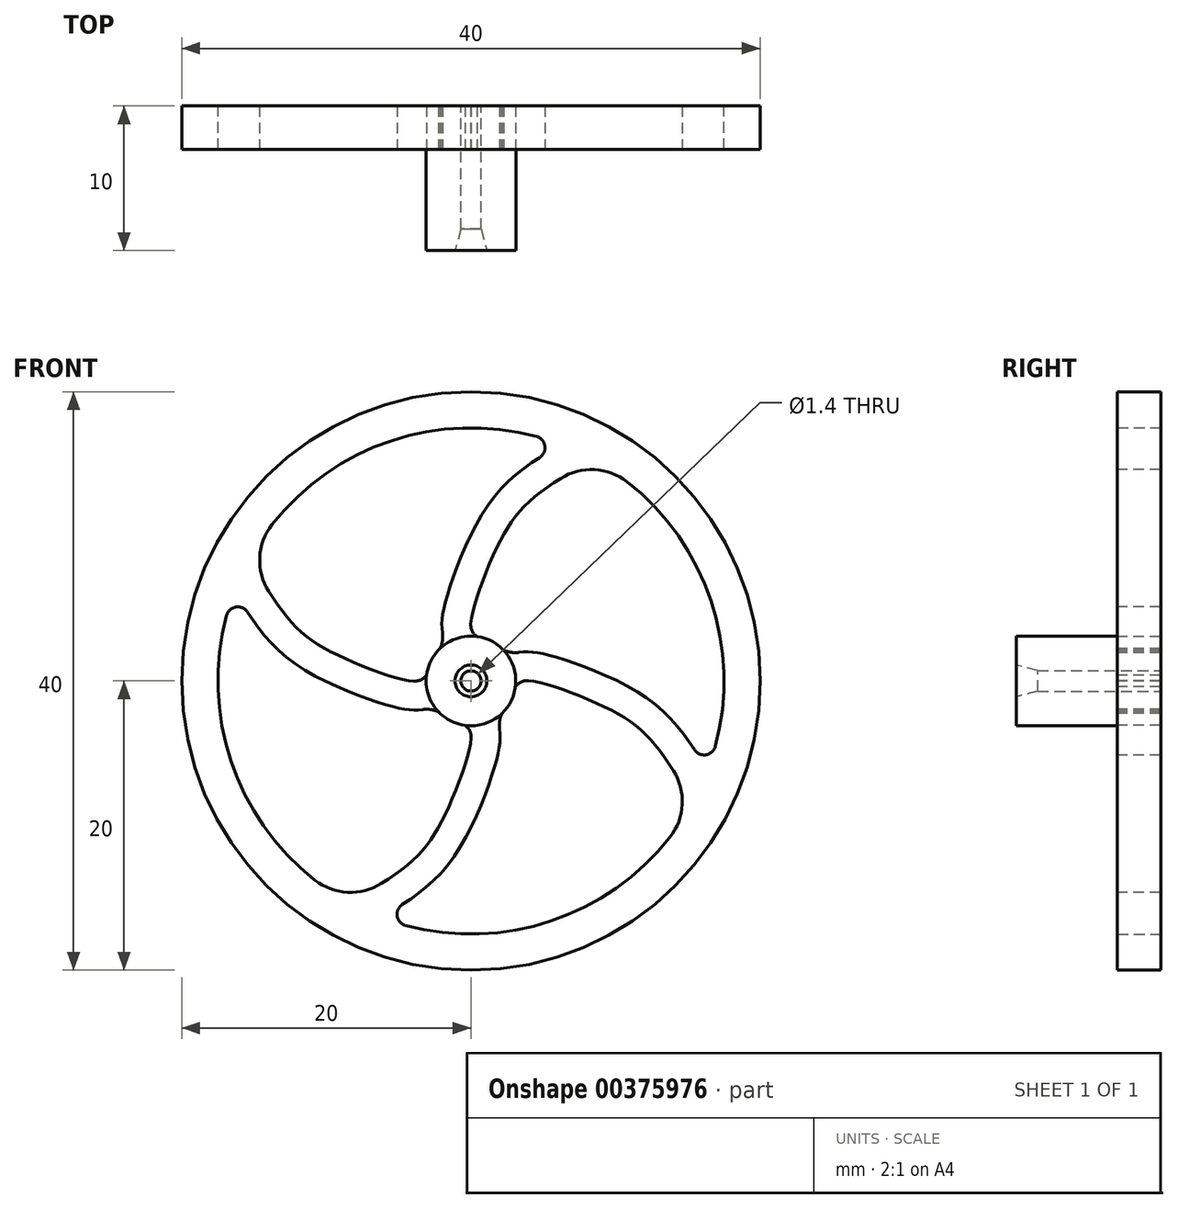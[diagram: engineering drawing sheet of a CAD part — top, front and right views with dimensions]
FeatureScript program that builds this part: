
annotation { "Feature Type Name" : "Feature", "Feature Type Description" : "" }
export const myFeature = defineFeature(function(context is Context, id is Id, definition is map)
    precondition{}
    {
        {
            var Q0;
            Q0=qCreatedBy(makeId("Front.planeOp"),FACE);
            var sketch = newSketch(context, id + "F0", { "sketchPlane" : qUnion([Q0])});
            skCircle(sketch, "E0", {"center": v(0, 0) * mm, "radius": 20 * mm});
            skCircle(sketch, "E1", {"center": v(0, 0) * mm, "radius": 0.7 * mm});
            skCircle(sketch, "E2", {"center": v(0, 0) * mm, "radius": 3.1 * mm});
            skCircle(sketch, "E3", {"center": v(0, 0) * mm, "radius": 17.5 * mm});
            skSolve(sketch);
        }
        {
            var Q0;
            Q0=qSketchRegion(id+"F0",true);
            var Q1;
            Q1=makeQuery(id+"F0.imprint","IMPRINT",FACE,{"disambiguationData":[TD([[makeQuery(id+"F0.imprint","IMPRINT",EDGE,{"derivedFrom":sQuery(id+"F0.wireOp",EDGE,"E1")}),-1.0]])]});
            extrude(context, id + "F1", {"entities" : qUnion([Q0, Q1]), "depth" : 3 * mm});
        }
        {
            var Q0;
            Q0=qCreatedBy(makeId("Right.planeOp"),FACE);
            var sketch = newSketch(context, id + "F2", { "sketchPlane" : qUnion([Q0])});
            skLineSegment(sketch, "E4", {"start": v(0, 17.54) * mm, "end": v(2.14, 1.57) * mm});
            skLineSegment(sketch, "E5", {"start": v(2.14, 1.57) * mm, "end": v(5.63, 1.57) * mm});
            skLineSegment(sketch, "E6", {"start": v(5.63, 1.57) * mm, "end": v(5.63, 19) * mm});
            skLineSegment(sketch, "E7", {"start": v(5.63, 19) * mm, "end": v(0, 19) * mm});
            skLineSegment(sketch, "E8", {"start": v(0, 19) * mm, "end": v(0, 17.54) * mm});
            skLineSegment(sketch, "E9", {"start": v(-16.5, 0) * mm, "end": v(18.02, 0) * mm});
            skLineSegment(sketch, "E10", {"start": v(18.02, 0) * mm, "end": v(18.02, 0.48) * mm});
            skSolve(sketch);
        }
        {
            var Q0;
            Q0=qSketchRegion(id+"F2",true);
            var Q1;
            Q1=sQuery(id+"F2.wireOp",EDGE,"E9");
            revolve(context, id + "F3", {"operationType" : NewBodyOperationType.REMOVE, "entities" : qUnion([Q0]), "axis" : qUnion([Q1]), "revolveType" : RevolveType.FULL});
        }
        {
            var Q0;
            Q0=makeQuery(id+"F1.opExtrude","CAP_FACE",FACE,{"disambiguationData":[OSD([sQuery(id+"F0.wireOp",EDGE,"E0"),sQuery(id+"F0.wireOp",EDGE,"E3")])],"isStart":false});
            var sketch = newSketch(context, id + "F4", { "sketchPlane" : qUnion([Q0])});
            skFitSpline(sketch, "E11", {"points": [v(-1.82, 2.4) * mm, v(-2, 3.75) * mm, v(-1.7, 5.68) * mm, v(1.39, 12.44) * mm, v(6.22, 16.36) * mm], "startDerivative": vector(-1.76, 9.05) * mm, "endDerivative": vector(16.16, 9.6) * mm});
            skFitSpline(sketch, "E12", {"points": [v(0.11, 2.97) * mm, v(0, 4.12) * mm, v(1.76, 9.17) * mm, v(4.06, 12.43) * mm, v(8.43, 15.33) * mm], "startDerivative": vector(-1.88, 6.55) * mm, "endDerivative": vector(16.22, 9.41) * mm});
            skArc(sketch, "E13.filletArc", {"start": v(10.8, 13.76) * mm, "mid": v(8.54, 14.61) * mm, "end": v(6.2, 14) * mm});
            skArc(sketch, "E14.filletArc", {"start": v(4.75, 15.46) * mm, "mid": v(5.11, 16.26) * mm, "end": v(4.53, 16.9) * mm});
            skArc(sketch, "E15.filletArc", {"start": v(-2.38, 1.85) * mm, "mid": v(-2.03, 2.54) * mm, "end": v(-1.97, 3.32) * mm});
            skPoint(sketch, "E16.visualSharp", {"position": v(0.1, 3) * mm});
            skArc(sketch, "E16.filletArc", {"start": v(-0.02, 3.96) * mm, "mid": v(0.17, 3.3) * mm, "end": v(0.74, 2.92) * mm});
            skArc(sketch, "E17", {"start": v(10.8, 13.76) * mm, "mid": v(7.83, 15.65) * mm, "end": v(4.53, 16.9) * mm});
            skArc(sketch, "E18", {"start": v(0.74, 2.92) * mm, "mid": v(-0.98, 2.85) * mm, "end": v(-2.38, 1.85) * mm});
            skSolve(sketch);
        }
        {
            var Q0;
            Q0=qSketchRegion(id+"F4",true);
            extrude(context, id + "F5", {"entities" : qUnion([Q0]), "oppositeDirection" : true, "depth" : 3 * mm});
        }
        {
            var Q0;
            Q0=makeQuery(id+"F5.opExtrude","SWEPT_BODY",BODY,{"disambiguationData":[OSD([sQuery(id+"F4.wireOp",EDGE,"E11"),sQuery(id+"F4.wireOp",EDGE,"E12"),sQuery(id+"F4.wireOp",EDGE,"E13.filletArc"),sQuery(id+"F4.wireOp",EDGE,"E14.filletArc"),sQuery(id+"F4.wireOp",EDGE,"E15.filletArc"),sQuery(id+"F4.wireOp",EDGE,"E16.filletArc"),sQuery(id+"F4.wireOp",EDGE,"E17"),sQuery(id+"F4.wireOp",EDGE,"E18")])]});
            var Q1;
            Q1=makeQuery(id+"F1.opExtrude","CAP_EDGE",EDGE,{"disambiguationData":[OSD([sQuery(id+"F0.wireOp",EDGE,"E0")])],"isStart":false});
            circularPattern(context, id + "F6", {"operationType" : NewBodyOperationType.ADD, "entities" : qUnion([Q0]), "axis" : qUnion([Q1]), "angle" : 360 * degree, "instanceCount" : 4, "equalSpace" : true});
        }
        {
            var Q0;
            Q0=makeQuery(id+"F1.opExtrude","CAP_FACE",FACE,{"disambiguationData":[OSD([sQuery(id+"F0.wireOp",EDGE,"E1"),sQuery(id+"F0.wireOp",EDGE,"E2")])],"isStart":false});
            var sketch = newSketch(context, id + "F7", { "sketchPlane" : qUnion([Q0])});
            skCircle(sketch, "E19.0.0", {"center": v(0, 0) * mm, "radius": 3.1 * mm});
            skCircle(sketch, "E20.0", {"center": v(0, 0) * mm, "radius": 0.7 * mm});
            skSolve(sketch);
        }
        {
            var Q0;
            Q0 = qSketchRegion(id + "F7", true);
            extrude(context, id + "F8", {"entities" : qUnion([Q0]), "operationType" : NewBodyOperationType.ADD, "depth" : 7 * mm});
        }
        {
            var Q0;
            Q0=makeQuery(id+"F8.opExtrude","CAP_EDGE",EDGE,{"disambiguationData":[OSD([sQuery(id+"F7.wireOp",EDGE,"E20.0")])],"isStart":false});
            chamfer(context, id + "F9", {"entities" : qUnion([Q0]), "chamferType" : ChamferType.TWO_OFFSETS, "width1" : 1.5 * mm, "oppositeDirection" : false, "width2" : .4 * mm, "tangentPropagation" : true});
        }
    });
